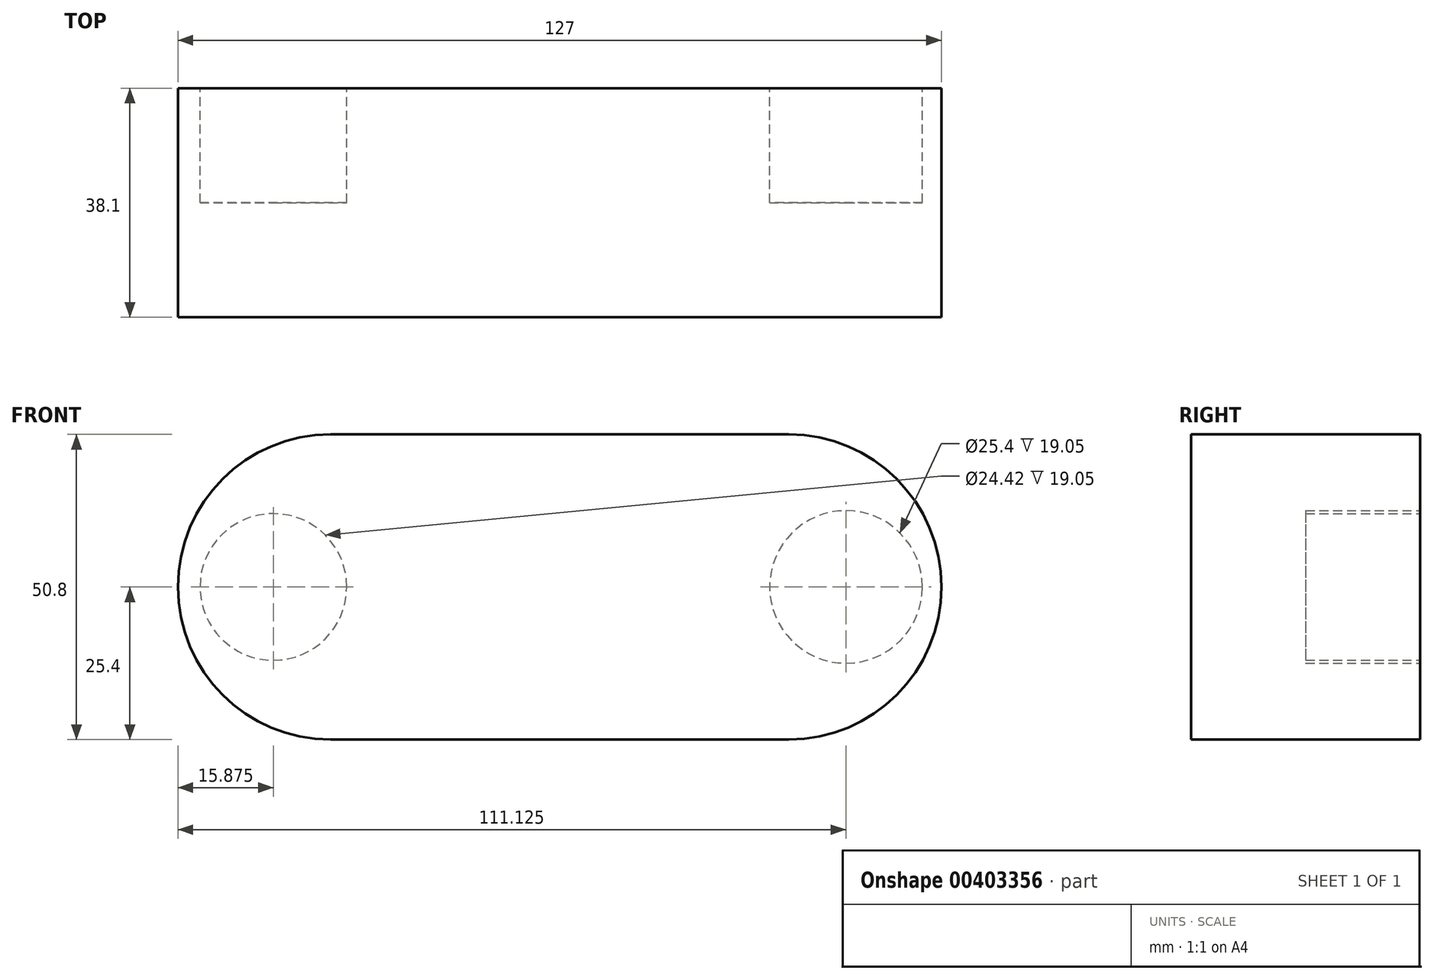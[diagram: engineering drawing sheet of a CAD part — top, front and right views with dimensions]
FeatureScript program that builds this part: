
annotation { "Feature Type Name" : "Feature", "Feature Type Description" : "" }
export const myFeature = defineFeature(function(context is Context, id is Id, definition is map)
    precondition{}
    {
        {
            var Q0;
            Q0=qCreatedBy(makeId("Front.planeOp"),FACE);
            var sketch = newSketch(context, id + "F0", { "sketchPlane" : qUnion([Q0])});
            skLineSegment(sketch, "E0.bottom", {"start": v(63.5, 25.4) * mm, "end": v(-63.5, 25.4) * mm});
            skLineSegment(sketch, "E0.top", {"start": v(63.5, -25.4) * mm, "end": v(-63.5, -25.4) * mm});
            skLineSegment(sketch, "E0.left", {"start": v(63.5, -25.4) * mm, "end": v(63.5, 25.4) * mm});
            skLineSegment(sketch, "E0.right", {"start": v(-63.5, -25.4) * mm, "end": v(-63.5, 25.4) * mm});
            skPoint(sketch, "E0.middle", {"position": v(0, 0) * mm});
            skSolve(sketch);
        }
        {
            var Q0;
            Q0=qSketchRegion(id+"F0",true);
            extrude(context, id + "F1", {"entities" : qUnion([Q0]), "depth" : 38.1 * mm});
        }
        {
            var Q0;
            Q0=makeQuery(id+"F1.opExtrude","SWEPT_EDGE",EDGE,{"disambiguationData":[OSD([sQuery(id+"F0.wireOp",EDGE,"E0.bottom"),sQuery(id+"F0.wireOp",EDGE,"E0.left")])]});
            var Q1;
            Q1=makeQuery(id+"F1.opExtrude","SWEPT_EDGE",EDGE,{"disambiguationData":[OSD([sQuery(id+"F0.wireOp",EDGE,"E0.top"),sQuery(id+"F0.wireOp",EDGE,"E0.left")])]});
            var Q2;
            Q2=makeQuery(id+"F1.opExtrude","SWEPT_EDGE",EDGE,{"disambiguationData":[OSD([sQuery(id+"F0.wireOp",EDGE,"E0.bottom"),sQuery(id+"F0.wireOp",EDGE,"E0.right")])]});
            var Q3;
            Q3=makeQuery(id+"F1.opExtrude","SWEPT_EDGE",EDGE,{"disambiguationData":[OSD([sQuery(id+"F0.wireOp",EDGE,"E0.top"),sQuery(id+"F0.wireOp",EDGE,"E0.right")])]});
            fillet(context, id + "F2", {"entities" : qUnion([Q0, Q1, Q2, Q3]), "radius" : 25.4 * mm, "tangentPropagation" : true, "allowEdgeOverflow" : false});
        }
        {
            var Q0;
            Q0=makeQuery(id+"F1.opExtrude","CAP_FACE",FACE,{"disambiguationData":[OSD([sQuery(id+"F0.wireOp",EDGE,"E0.bottom"),sQuery(id+"F0.wireOp",EDGE,"E0.top"),sQuery(id+"F0.wireOp",EDGE,"E0.left"),sQuery(id+"F0.wireOp",EDGE,"E0.right")])],"isStart":true});
            var sketch = newSketch(context, id + "F3", { "sketchPlane" : qUnion([Q0])});
            skCircle(sketch, "E1", {"center": v(47.62, 0) * mm, "radius": 12.2 * mm});
            skCircle(sketch, "E2", {"center": v(-47.62, 0) * mm, "radius": 12.7 * mm});
            skSolve(sketch);
        }
        {
            var Q0;
            Q0=qSketchRegion(id+"F3",true);
            extrude(context, id + "F4", {"entities" : qUnion([Q0]), "operationType" : NewBodyOperationType.REMOVE, "oppositeDirection" : true, "depth" : 19.05 * mm});
        }
    });
